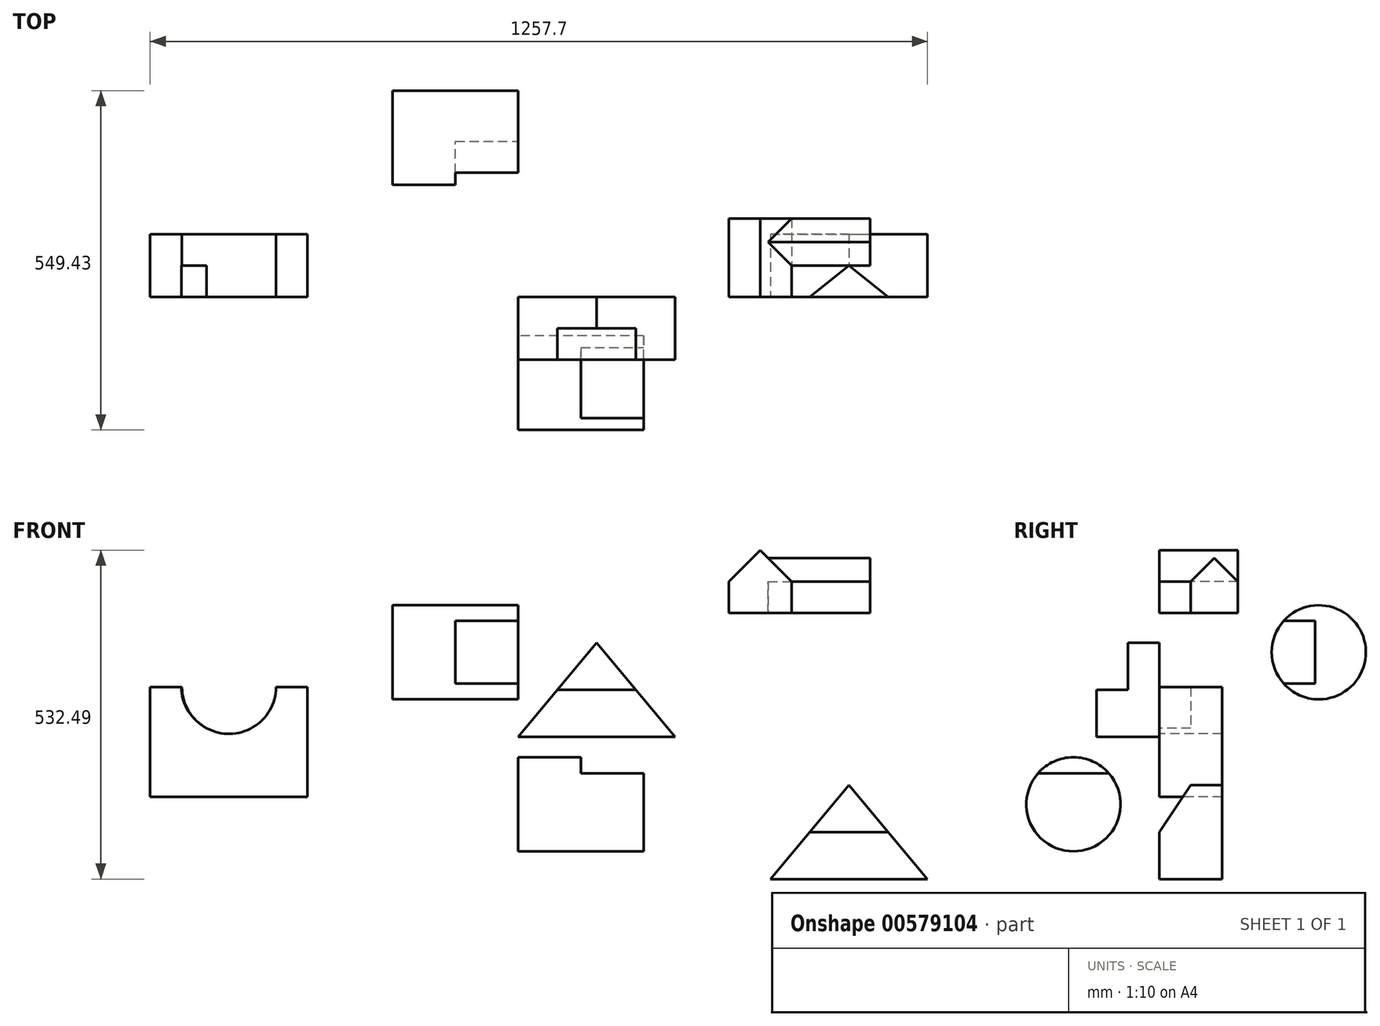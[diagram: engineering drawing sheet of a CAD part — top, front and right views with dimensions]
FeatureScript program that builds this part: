
annotation { "Feature Type Name" : "Feature", "Feature Type Description" : "" }
export const myFeature = defineFeature(function(context is Context, id is Id, definition is map)
    precondition{}
    {
        {
            var Q0;
            Q0=qCreatedBy(makeId("Front.planeOp"),FACE);
            var sketch = newSketch(context, id + "F0", { "sketchPlane" : qUnion([Q0])});
            skLineSegment(sketch, "E0.bottom", {"start": v(0, 0) * mm, "end": v(254, 0) * mm});
            skLineSegment(sketch, "E1", {"start": v(0, 0) * mm, "end": v(127, 152.4) * mm});
            skLineSegment(sketch, "E2", {"start": v(127, 152.4) * mm, "end": v(254, 0) * mm});
            skPoint(sketch, "E3.orphan", {"position": v(254, 152.4) * mm});
            skPoint(sketch, "E0.top.start.orphan", {"position": v(0, 152.4) * mm});
            skPoint(sketch, "E4.orphan", {"position": v(0, 76.2) * mm});
            skPoint(sketch, "E5.orphan", {"position": v(254, 76.2) * mm});
            skSolve(sketch);
        }
        {
            var Q0;
            Q0=makeQuery(id+"F0.imprint","IMPRINT",FACE,{"disambiguationData":[TD([[makeQuery(id+"F0.imprint","IMPRINT",EDGE,{"derivedFrom":sQuery(id+"F0.wireOp",EDGE,"E0.bottom")}),1.0]])]});
            extrude(context, id + "F1", {"entities" : qUnion([Q0]), "depth" : 101.6 * mm, "offsetDistance" : 25.4 * mm});
        }
        {
            var Q0;
            Q0=makeQuery(id+"F1.opExtrude","CAP_FACE",FACE,{"disambiguationData":[OSD([sQuery(id+"F0.wireOp",EDGE,"E0.bottom"),sQuery(id+"F0.wireOp",EDGE,"E1"),sQuery(id+"F0.wireOp",EDGE,"E2")])],"isStart":false});
            var sketch = newSketch(context, id + "F2", { "sketchPlane" : qUnion([Q0])});
            skLineSegment(sketch, "E6", {"start": v(127, 152.4) * mm, "end": v(63.5, 76.2) * mm});
            skLineSegment(sketch, "E7", {"start": v(63.5, 76.2) * mm, "end": v(190.5, 76.2) * mm});
            skLineSegment(sketch, "E8", {"start": v(190.5, 76.2) * mm, "end": v(127, 152.4) * mm});
            skSolve(sketch);
        }
        {
            var Q0;
            Q0=makeQuery(id+"F2.imprint","IMPRINT",FACE,{"disambiguationData":[TD([[makeQuery(id+"F2.imprint","IMPRINT",EDGE,{"derivedFrom":sQuery(id+"F2.wireOp",EDGE,"E6")}),-1.0]])]});
            extrude(context, id + "F3", {"entities" : qUnion([Q0]), "operationType" : NewBodyOperationType.REMOVE, "oppositeDirection" : true, "depth" : 50.8 * mm, "offsetDistance" : 25.4 * mm});
        }
        {
            var Q0;
            Q0=qCreatedBy(makeId("Front.planeOp"),FACE);
            var sketch = newSketch(context, id + "F4", { "sketchPlane" : qUnion([Q0])});
            skLineSegment(sketch, "E9.bottom", {"start": v(408.46, -230.28) * mm, "end": v(662.46, -230.28) * mm});
            skLineSegment(sketch, "E9.top", {"start": v(408.46, -77.88) * mm, "end": v(662.46, -77.88) * mm});
            skLineSegment(sketch, "E9.left", {"start": v(408.46, -230.28) * mm, "end": v(408.46, -77.88) * mm});
            skLineSegment(sketch, "E9.right", {"start": v(662.46, -230.28) * mm, "end": v(662.46, -77.88) * mm});
            skLineSegment(sketch, "E10", {"start": v(535.46, -77.88) * mm, "end": v(408.46, -230.28) * mm});
            skLineSegment(sketch, "E11", {"start": v(535.46, -77.88) * mm, "end": v(662.46, -230.28) * mm});
            skSolve(sketch);
        }
        {
            var Q0;
            Q0=makeQuery(id+"F4.imprint","IMPRINT",FACE,{"disambiguationData":[TD([[makeQuery(id+"F4.imprint","IMPRINT",EDGE,{"derivedFrom":sQuery(id+"F4.wireOp",EDGE,"E9.bottom")}),1.0]])]});
            extrude(context, id + "F5", {"entities" : qUnion([Q0]), "oppositeDirection" : true, "depth" : 101.6 * mm, "offsetDistance" : 25.4 * mm});
        }
        {
            var Q0;
            Q0=makeQuery(id+"F5.opExtrude","CAP_EDGE",EDGE,{"disambiguationData":[OSD([sQuery(id+"F4.wireOp",EDGE,"E9.bottom")])],"isStart":true});
            cPoint(context, id + "F6", {"entities" : qUnion([Q0]), "parameter" : 0.5});
        }
        {
            var Q0;
            Q0=makeQuery(id+"F5.opExtrude","CAP_VERTEX",VERTEX,{"disambiguationData":[OSD([sQuery(id+"F4.wireOp",EDGE,"E9.top"),sQuery(id+"F4.wireOp",EDGE,"E10"),sQuery(id+"F4.wireOp",EDGE,"E11")])],"isStart":true});
            var Q1;
            Q1=makeQuery(id+"F5.opExtrude","CAP_VERTEX",VERTEX,{"disambiguationData":[OSD([sQuery(id+"F4.wireOp",EDGE,"E9.top"),sQuery(id+"F4.wireOp",EDGE,"E10"),sQuery(id+"F4.wireOp",EDGE,"E11")])],"isStart":false});
            var Q2;
            Q2 = qCreatedBy(id + "F6" ,VERTEX);
            cPlane(context, id + "F7", {"entities" : qUnion([Q0, Q1, Q2]), "cplaneType" : CPlaneType.THREE_POINT, "offset" : 25.4 * mm, "width" : 152.4 * mm, "height" : 152.4 * mm});
        }
        {
            var Q0;
            Q0=qCreatedBy(id+"F7.planeOp",FACE);
            var sketch = newSketch(context, id + "F8", { "sketchPlane" : qUnion([Q0])});
            skPoint(sketch, "E12.0", {"position": v(0, -77.88) * mm});
            skPoint(sketch, "E13.0", {"position": v(50.8, -77.88) * mm});
            skPoint(sketch, "E14.0", {"position": v(0, -154.08) * mm});
            skLineSegment(sketch, "E15", {"start": v(0, -77.88) * mm, "end": v(0, -154.08) * mm});
            skLineSegment(sketch, "E16", {"start": v(50.8, -77.88) * mm, "end": v(0, -154.08) * mm});
            skLineSegment(sketch, "E17", {"start": v(0, -77.88) * mm, "end": v(50.8, -77.88) * mm});
            skSolve(sketch);
        }
        {
            var Q0;
            Q0 = qSketchRegion(id + "F8", true);
            extrude(context, id + "F9", {"entities" : qUnion([Q0]), "operationType" : NewBodyOperationType.REMOVE, "endBound" : BoundingType.SYMMETRIC, "depth" : 127 * mm, "offsetDistance" : 25.4 * mm});
        }
        {
            var Q0;
            Q0=qCreatedBy(makeId("Front.planeOp"),FACE);
            var sketch = newSketch(context, id + "F10", { "sketchPlane" : qUnion([Q0])});
            skLineSegment(sketch, "E18", {"start": v(341.35, 200.6) * mm, "end": v(442.95, 200.6) * mm});
            skLineSegment(sketch, "E19", {"start": v(442.95, 200.6) * mm, "end": v(442.95, 251.4) * mm});
            skLineSegment(sketch, "E20", {"start": v(341.35, 200.6) * mm, "end": v(341.35, 251.4) * mm});
            skLineSegment(sketch, "E21", {"start": v(341.35, 251.4) * mm, "end": v(392.15, 302.2) * mm});
            skPoint(sketch, "E21.endSnap0", {"position": v(392.15, 200.6) * mm});
            skLineSegment(sketch, "E22", {"start": v(392.15, 302.2) * mm, "end": v(442.95, 251.4) * mm});
            skLineSegment(sketch, "E23", {"start": v(442.95, 251.4) * mm, "end": v(569.95, 251.4) * mm});
            skLineSegment(sketch, "E24", {"start": v(569.95, 251.4) * mm, "end": v(569.95, 200.6) * mm});
            skLineSegment(sketch, "E25", {"start": v(569.95, 200.6) * mm, "end": v(442.95, 200.6) * mm});
            skSolve(sketch);
        }
        {
            var Q0;
            Q0=makeQuery(id+"F10.imprint","IMPRINT",FACE,{"disambiguationData":[TD([[makeQuery(id+"F10.imprint","IMPRINT",EDGE,{"derivedFrom":sQuery(id+"F10.wireOp",EDGE,"E18")}),1.0]])]});
            extrude(context, id + "F11", {"entities" : qUnion([Q0]), "oppositeDirection" : true, "depth" : 127 * mm, "offsetDistance" : 25.4 * mm});
        }
        {
            var Q0;
            Q0=makeQuery(id+"F11.opExtrude","SWEPT_FACE",FACE,{"disambiguationData":[OSD([sQuery(id+"F10.wireOp",EDGE,"E19")])]});
            cPlane(context, id + "F12", {"entities" : qUnion([Q0]), "cplaneType" : CPlaneType.OFFSET, "offset" : 127 * mm, "width" : 152.4 * mm, "height" : 152.4 * mm});
        }
        {
            var Q0;
            Q0=qCreatedBy(id+"F12.planeOp",FACE);
            var sketch = newSketch(context, id + "F13", { "sketchPlane" : qUnion([Q0])});
            skLineSegment(sketch, "E26", {"start": v(127.1, 200.8) * mm, "end": v(50.9, 200.8) * mm});
            skLineSegment(sketch, "E27", {"start": v(50.9, 200.8) * mm, "end": v(50.9, 251.6) * mm});
            skLineSegment(sketch, "E28", {"start": v(50.9, 251.6) * mm, "end": v(89, 289.7) * mm});
            skPoint(sketch, "E28.endSnap0", {"position": v(89, 200.8) * mm});
            skLineSegment(sketch, "E29", {"start": v(89, 289.7) * mm, "end": v(127.1, 251.6) * mm});
            skLineSegment(sketch, "E30", {"start": v(127.1, 251.6) * mm, "end": v(127.1, 200.8) * mm});
            skSolve(sketch);
        }
        {
            var Q0;
            Q0=makeQuery(id+"F13.imprint","IMPRINT",FACE,{"disambiguationData":[TD([[makeQuery(id+"F13.imprint","IMPRINT",EDGE,{"derivedFrom":sQuery(id+"F13.wireOp",EDGE,"E26")}),-1.0]])]});
            extrude(context, id + "F14", {"entities" : qUnion([Q0]), "operationType" : NewBodyOperationType.ADD, "oppositeDirection" : true, "depth" : 165.1 * mm, "offsetDistance" : 25.4 * mm});
        }
        {
            var Q0;
            Q0=qCreatedBy(makeId("Right.planeOp"),FACE);
            var sketch = newSketch(context, id + "F15", { "sketchPlane" : qUnion([Q0])});
            skCircle(sketch, "E31", {"center": v(-139.07, -109.23) * mm, "radius": 76.2 * mm});
            skSolve(sketch);
        }
        {
            var Q0;
            Q0=makeQuery(id+"F15.imprint","IMPRINT",FACE,{"disambiguationData":[TD([[makeQuery(id+"F15.imprint","IMPRINT",EDGE,{"derivedFrom":sQuery(id+"F15.wireOp",EDGE,"E31")}),1.0]])]});
            extrude(context, id + "F16", {"entities" : qUnion([Q0]), "depth" : 203.2 * mm, "offsetDistance" : 25.4 * mm});
        }
        {
            var Q0;
            Q0=makeQuery(id+"F16.opExtrude","CAP_FACE",FACE,{"disambiguationData":[OSD([sQuery(id+"F15.wireOp",EDGE,"E31")])],"isStart":false});
            var sketch = newSketch(context, id + "F17", { "sketchPlane" : qUnion([Q0])});
            skLineSegment(sketch, "E32", {"start": v(-196.22, -58.83) * mm, "end": v(-81.92, -58.83) * mm});
            skSolve(sketch);
        }
        {
            var Q0;
            {var subQ0=sQuery(id+"F17.wireOp",EDGE,"E32");Q0=makeQuery(id+"F17.imprint","IMPRINT",FACE,{"disambiguationData":[TD([[makeQuery(id+"F17.imprint","IMPRINT",EDGE,{"derivedFrom":subQ0}),1.0]])]});}
            extrude(context, id + "F18", {"entities" : qUnion([Q0]), "operationType" : NewBodyOperationType.REMOVE, "oppositeDirection" : true, "depth" : 101.6 * mm, "offsetDistance" : 25.4 * mm});
        }
        {
            var Q0;
            Q0=qCreatedBy(makeId("Right.planeOp"),FACE);
            var sketch = newSketch(context, id + "F19", { "sketchPlane" : qUnion([Q0])});
            skCircle(sketch, "E33", {"center": v(257.96, 136.95) * mm, "radius": 76.2 * mm});
            skSolve(sketch);
        }
        {
            var Q0;
            Q0 = qSketchRegion(id + "F19", true);
            extrude(context, id + "F20", {"entities" : qUnion([Q0]), "oppositeDirection" : true, "depth" : 203.2 * mm, "offsetDistance" : 25.4 * mm});
        }
        {
            var Q0;
            Q0=makeQuery(id+"F20.opExtrude","CAP_FACE",FACE,{"disambiguationData":[OSD([sQuery(id+"F19.wireOp",EDGE,"E33")])],"isStart":true});
            var sketch = newSketch(context, id + "F21", { "sketchPlane" : qUnion([Q0])});
            skLineSegment(sketch, "E34", {"start": v(201.16, 187.75) * mm, "end": v(251.96, 187.75) * mm});
            skLineSegment(sketch, "E35", {"start": v(251.96, 187.75) * mm, "end": v(251.96, 86.15) * mm});
            skLineSegment(sketch, "E36", {"start": v(251.96, 86.15) * mm, "end": v(201.16, 86.15) * mm});
            skSolve(sketch);
        }
        {
            var Q0;
            {var subQ0=sQuery(id+"F21.wireOp",EDGE,"E34");Q0=makeQuery(id+"F21.imprint","IMPRINT",FACE,{"disambiguationData":[TD([[makeQuery(id+"F21.imprint","IMPRINT",EDGE,{"derivedFrom":subQ0}),-1.0]])]});}
            extrude(context, id + "F22", {"entities" : qUnion([Q0]), "operationType" : NewBodyOperationType.REMOVE, "oppositeDirection" : true, "depth" : 101.6 * mm, "offsetDistance" : 25.4 * mm});
        }
        {
            var Q0;
            Q0=qCreatedBy(makeId("Front.planeOp"),FACE);
            var sketch = newSketch(context, id + "F23", { "sketchPlane" : qUnion([Q0])});
            skLineSegment(sketch, "E37.bottom", {"start": v(-595.24, 80.62) * mm, "end": v(-341.24, 80.62) * mm});
            skLineSegment(sketch, "E37.top", {"start": v(-595.24, -97.18) * mm, "end": v(-341.24, -97.18) * mm});
            skLineSegment(sketch, "E37.left", {"start": v(-595.24, 80.62) * mm, "end": v(-595.24, -97.18) * mm});
            skLineSegment(sketch, "E37.right", {"start": v(-341.24, 80.62) * mm, "end": v(-341.24, -97.18) * mm});
            skCircle(sketch, "E38", {"center": v(-467.8, 81.08) * mm, "radius": 76.2 * mm});
            skPoint(sketch, "E38.first.point", {"position": v(-544, 80.62) * mm});
            skPoint(sketch, "E38.second.point", {"position": v(-393.96, 62.24) * mm});
            skSolve(sketch);
        }
        {
            var Q0;
            {var subQ0=sQuery(id+"F23.wireOp",EDGE,"E38");var subQ1=sQuery(id+"F23.wireOp",EDGE,"E37.bottom");var subQ2=makeQuery(id+"F23.imprint","INTERSECT",VERTEX,{"disambiguationData":[OD(0.0)],"derivedFrom":[subQ1,subQ0]});Q0=makeQuery(id+"F23.imprint","IMPRINT",FACE,{"disambiguationData":[TD([[makeQuery(id+"F23.imprint","IMPRINT",EDGE,{"disambiguationData":[TD([[subQ2,-1.0]])],"derivedFrom":subQ1}),-1.0]])]});}
            var Q1;
            Q1=makeQuery(id+"F23.imprint","IMPRINT",FACE,{"disambiguationData":[TD([[makeQuery(id+"F23.imprint","IMPRINT",EDGE,{"derivedFrom":sQuery(id+"F23.wireOp",EDGE,"E37.top")}),1.0]])]});
            extrude(context, id + "F24", {"entities" : qUnion([Q0, Q1]), "oppositeDirection" : true, "depth" : 101.6 * mm, "offsetDistance" : 25.4 * mm});
        }
        {
            var Q0;
            Q0=makeQuery(id+"F24.opExtrude","CAP_FACE",FACE,{"disambiguationData":[OSD([sQuery(id+"F23.wireOp",EDGE,"E37.bottom"),sQuery(id+"F23.wireOp",EDGE,"E37.top"),sQuery(id+"F23.wireOp",EDGE,"E37.left"),sQuery(id+"F23.wireOp",EDGE,"E37.right")])],"isStart":true});
            var sketch = newSketch(context, id + "F25", { "sketchPlane" : qUnion([Q0])});
            skCircle(sketch, "E39", {"center": v(-468.9, 81.67) * mm, "radius": 76.2 * mm});
            skPoint(sketch, "E39.first.point", {"position": v(-545.1, 80.62) * mm});
            skPoint(sketch, "E39.second.point", {"position": v(-393.6, 93.36) * mm});
            skPoint(sketch, "E39.third.point", {"position": v(-393.1, 73.83) * mm});
            skSolve(sketch);
        }
        {
            var Q0;
            {var subQ0=sQuery(id+"F25.wireOp",EDGE,"E39");var subQ1=makeQuery(id+"F24.opExtrude","CAP_EDGE",EDGE,{"disambiguationData":[OSD([sQuery(id+"F23.wireOp",EDGE,"E37.bottom")])],"isStart":true});var subQ2=makeQuery(id+"F25.imprint","INTERSECT",VERTEX,{"disambiguationData":[OD(0.0)],"derivedFrom":[subQ1,subQ0]});Q0=makeQuery(id+"F25.imprint","IMPRINT",FACE,{"disambiguationData":[TD([[makeQuery(id+"F25.imprint","IMPRINT",EDGE,{"disambiguationData":[TD([[subQ2,-1.0]])],"derivedFrom":subQ0}),1.0]])]});}
            extrude(context, id + "F26", {"entities" : qUnion([Q0]), "operationType" : NewBodyOperationType.REMOVE, "oppositeDirection" : true, "depth" : 50.8 * mm, "offsetDistance" : 25.4 * mm});
        }
    });
